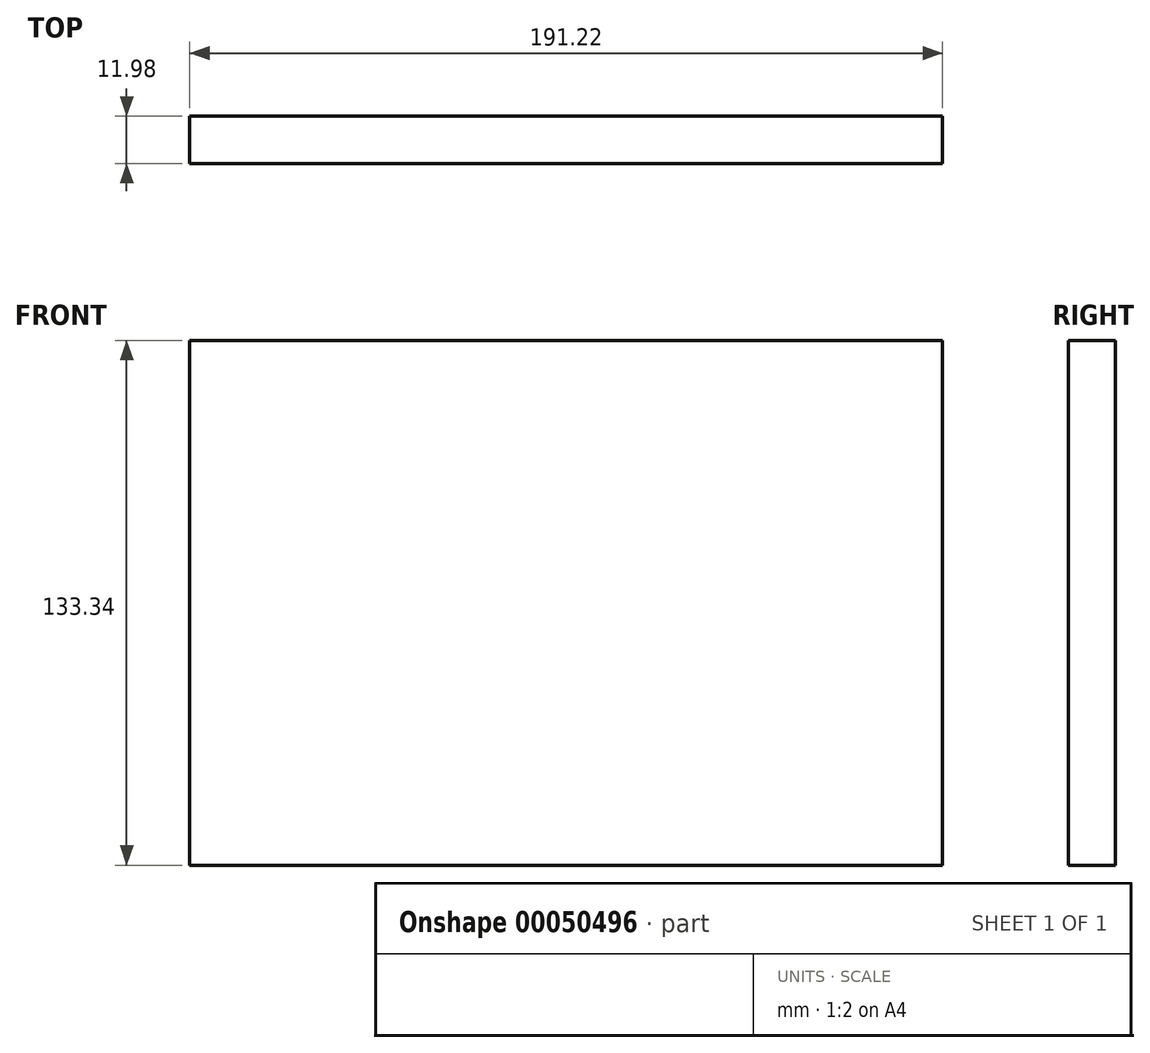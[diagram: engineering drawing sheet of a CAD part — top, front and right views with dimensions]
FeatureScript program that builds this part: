
annotation { "Feature Type Name" : "Feature", "Feature Type Description" : "" }
export const myFeature = defineFeature(function(context is Context, id is Id, definition is map)
    precondition{}
    {
        {
            var Q0;
            Q0=qCreatedBy(makeId("Front.planeOp"),FACE);
            var sketch = newSketch(context, id + "F0", { "sketchPlane" : qUnion([Q0])});
            skLineSegment(sketch, "E0.rect.bottom", {"start": v(95.6, 66.68) * mm, "end": v(-95.6, 66.68) * mm});
            skLineSegment(sketch, "E0.rect.top", {"start": v(95.6, -66.68) * mm, "end": v(-95.6, -66.68) * mm});
            skLineSegment(sketch, "E0.rect.left", {"start": v(95.6, 66.68) * mm, "end": v(95.6, -66.67) * mm});
            skLineSegment(sketch, "E0.rect.right", {"start": v(-95.6, 66.68) * mm, "end": v(-95.6, -66.67) * mm});
            skPoint(sketch, "E0.rect.middle", {"position": v(0, 0) * mm});
            skSolve(sketch);
        }
        {
            var Q0;
            Q0 = qSketchRegion(id + "F0", true);
            extrude(context, id + "F1", {"entities" : qUnion([Q0]), "endBound" : BoundingType.SYMMETRIC, "depth" : 12 * mm});
        }
    });
